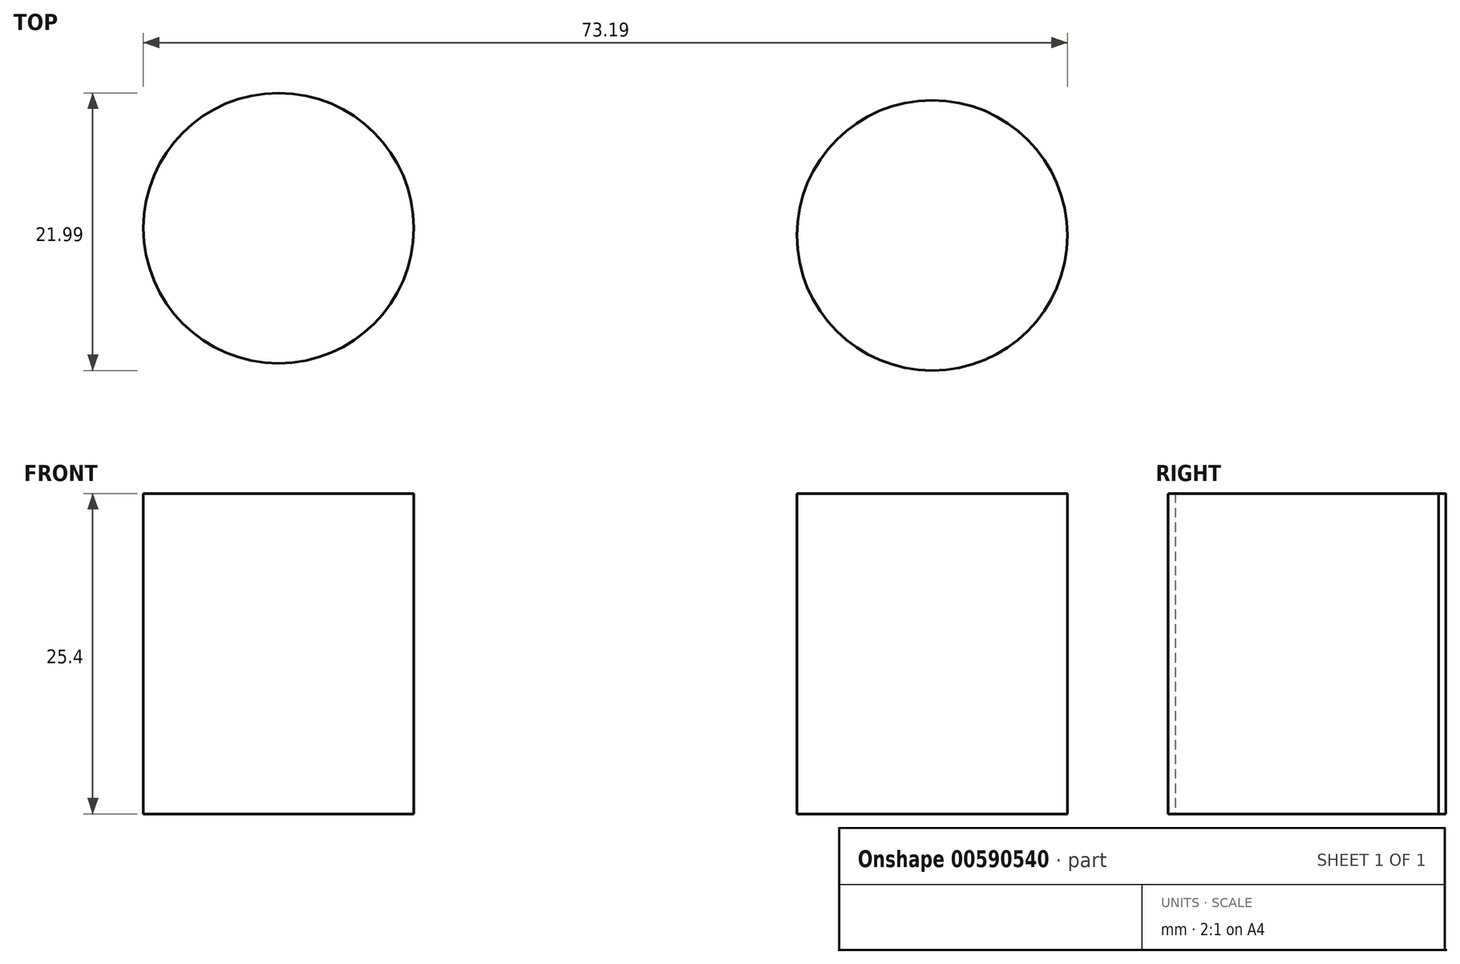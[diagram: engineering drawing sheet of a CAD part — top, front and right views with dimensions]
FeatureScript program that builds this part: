
annotation { "Feature Type Name" : "Feature", "Feature Type Description" : "" }
export const myFeature = defineFeature(function(context is Context, id is Id, definition is map)
    precondition{}
    {
        {
            var Q0;
            Q0=qCreatedBy(makeId("Top.planeOp"),FACE);
            var sketch = newSketch(context, id + "F0", { "sketchPlane" : qUnion([Q0])});
            skCircle(sketch, "E0", {"center": v(-24.78, 18.73) * mm, "radius": 10.71 * mm});
            skCircle(sketch, "E1", {"center": v(27, 18.16) * mm, "radius": 10.71 * mm});
            skCircle(sketch, "E2", {"center": v(1.54, 18.53) * mm, "radius": 10.71 * mm});
            skSolve(sketch);
        }
        {
            var Q0;
            Q0=makeQuery(id+"F0.imprint","IMPRINT",FACE,{"disambiguationData":[TD([[makeQuery(id+"F0.imprint","IMPRINT",EDGE,{"derivedFrom":sQuery(id+"F0.wireOp",EDGE,"E0")}),1.0]])]});
            var Q1;
            Q1=makeQuery(id+"F0.imprint","IMPRINT",FACE,{"disambiguationData":[TD([[makeQuery(id+"F0.imprint","IMPRINT",EDGE,{"derivedFrom":sQuery(id+"F0.wireOp",EDGE,"E1")}),1.0]])]});
            extrude(context, id + "F1", {"entities" : qUnion([Q0, Q1]), "depth" : 25.4 * mm, "offsetDistance" : 25.4 * mm});
        }
    });
